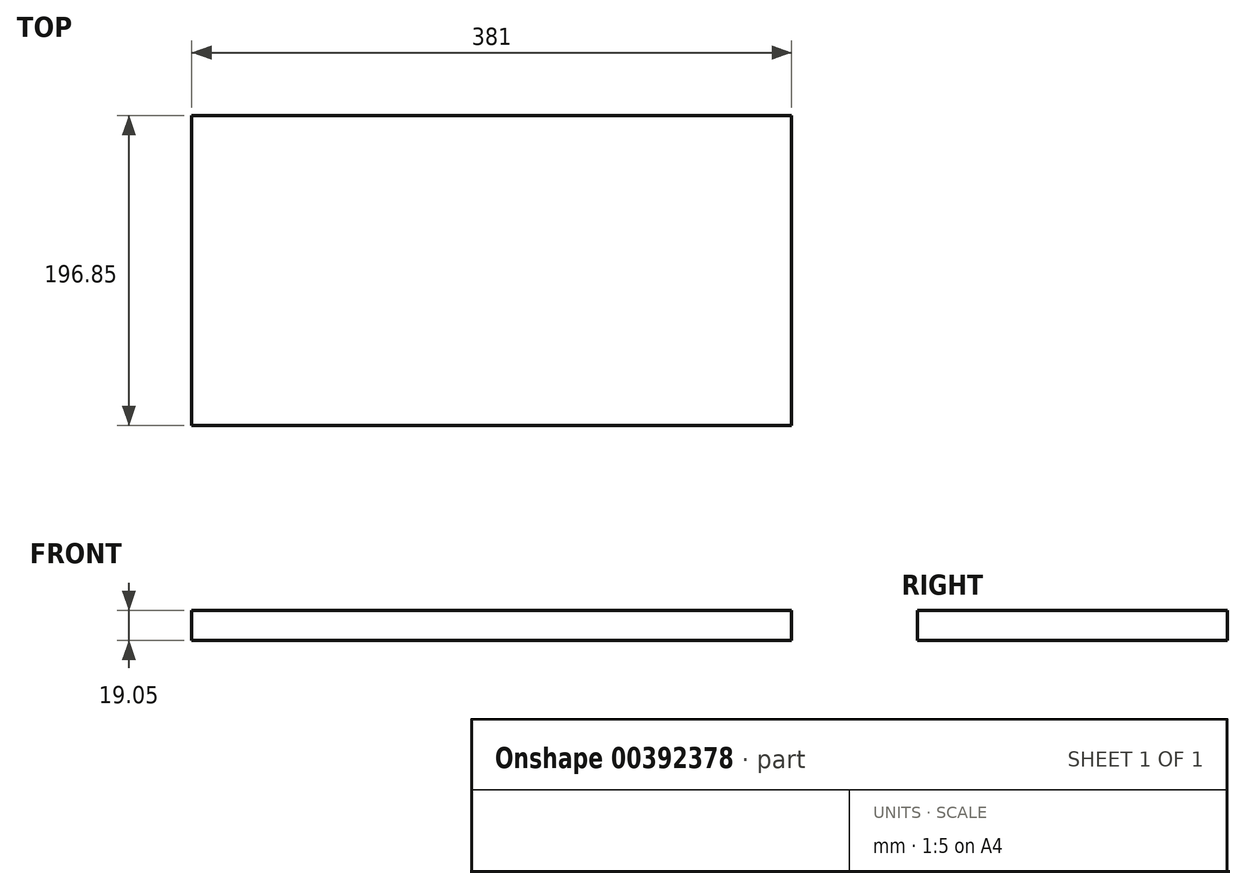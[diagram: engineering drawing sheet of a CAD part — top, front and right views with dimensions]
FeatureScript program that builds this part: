
annotation { "Feature Type Name" : "Feature", "Feature Type Description" : "" }
export const myFeature = defineFeature(function(context is Context, id is Id, definition is map)
    precondition{}
    {
        {
            var Q0;
            Q0=qCreatedBy(makeId("Top.planeOp"),FACE);
            var sketch = newSketch(context, id + "F0", { "sketchPlane" : qUnion([Q0])});
            skLineSegment(sketch, "E0.bottom", {"start": v(0, 0) * mm, "end": v(-381, 0) * mm});
            skLineSegment(sketch, "E0.top", {"start": v(0, -196.85) * mm, "end": v(-381, -196.85) * mm});
            skLineSegment(sketch, "E0.left", {"start": v(0, 0) * mm, "end": v(0, -196.85) * mm});
            skLineSegment(sketch, "E0.right", {"start": v(-381, 0) * mm, "end": v(-381, -196.85) * mm});
            skSolve(sketch);
        }
        {
            var Q0;
            Q0=makeQuery(id+"F0.imprint","IMPRINT",FACE,{"disambiguationData":[TD([[makeQuery(id+"F0.imprint","IMPRINT",EDGE,{"derivedFrom":sQuery(id+"F0.wireOp",EDGE,"E0.bottom")}),1.0]])]});
            extrude(context, id + "F1", {"entities" : qUnion([Q0]), "depth" : 19.05 * mm});
        }
    });
